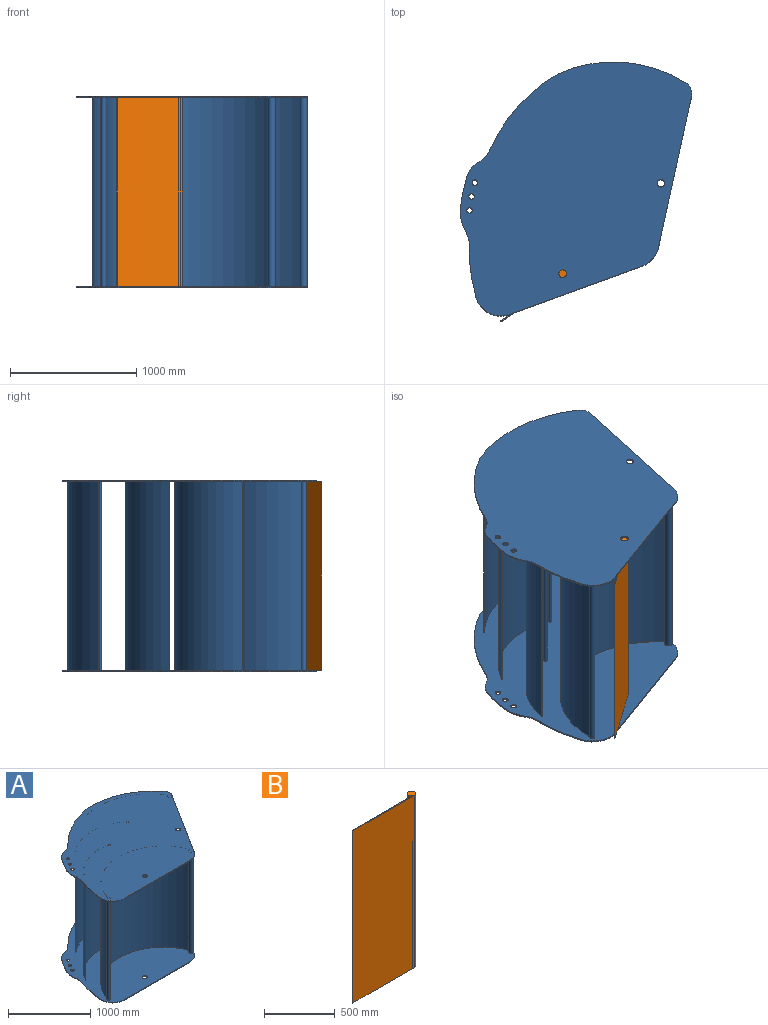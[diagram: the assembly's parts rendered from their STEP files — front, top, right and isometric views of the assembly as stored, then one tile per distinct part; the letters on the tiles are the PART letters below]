
ASSEMBLY  parts=2 mates=2
PART A: 61 faces, bbox 2164.2x1661x1520 mm
  f0: cylinder r=30.5mm len=61mm, axis (0,0,-1), area 1916.4mm2, adj f48,f49
  f1: cylinder r=29.5mm len=59mm, axis (0,0,-1), area 1853.5mm2, adj f48,f49
  f2: cylinder r=22mm len=44mm, axis (0,0,-1), area 1382.3mm2, adj f48,f49
  f3: cylinder r=22mm len=44mm, axis (0,0,-1), area 1382.3mm2, adj f48,f49
  f4: cylinder r=22mm len=44mm, axis (0,0,-1), area 1382.3mm2, adj f48,f49
  f5: cylinder r=326.18mm len=176.61mm, axis (0,0,-1), area 1797.7mm2, adj f48,f49,f50,f60
  f6: cylinder r=200mm len=212.82mm, axis (0,0,-1), area 3269.9mm2, adj f48,f49,f51,f52
  f7: cylinder r=20.5mm len=1500mm, axis (0,0,-1), area 183146.8mm2, adj f30,f44,f45,f49
  f8: cylinder r=30.5mm len=1500mm, axis (0,0,-1), area 272705.4mm2, adj f30,f44,f45,f46,f47,f49
  f9: cylinder r=15.5mm len=1500mm, axis (0,0,-1), area 135747.8mm2, adj f30,f41,f43,f49
  f10: cylinder r=15.5mm len=1500mm, axis (0,0,-1), area 136340.4mm2, adj f30,f37,f40,f49
  f11: cylinder r=30.5mm len=1500mm, axis (0,0,-1), area 274743.1mm2, adj f30,f32,f34,f35,f36,f49
  f12: cylinder r=30.5mm len=61mm, axis (0,0,-1), area 1916.4mm2, adj f30,f31
  f13: cylinder r=22mm len=44mm, axis (0,0,-1), area 1382.3mm2, adj f30,f31
  f14: cylinder r=22mm len=44mm, axis (0,0,-1), area 1382.3mm2, adj f30,f31
  f15: cylinder r=22mm len=44mm, axis (0,0,-1), area 1382.3mm2, adj f30,f31
  f16: cylinder r=29.5mm len=59mm, axis (0,0,-1), area 1853.5mm2, adj f30,f31
  f17: cylinder r=326.18mm len=176.61mm, axis (0,0,-1), area 1797.7mm2, adj f28,f29,f30,f31
  f18: cylinder r=200mm len=212.82mm, axis (0,0,-1), area 3269.9mm2, adj f19,f20,f30,f31
  f19: cylinder r=1403.06mm len=415.74mm, axis (0,0,-1), area 4273.2mm2, adj f18,f29,f30,f31
  f20: plane 1123.76x10mm, normal (0,-1,0), area 11237.6mm2, adj f18,f21,f30,f31
  f21: cylinder r=200mm len=169mm, axis (0,0,-1), area 2013.2mm2, adj f20,f22,f30,f31
  f22: plane 1036.5x655.9mm, normal (0.85,-0.53,0), area 12265.9mm2, adj f21,f23,f30,f31,f36,f47
  f23: cylinder r=100mm len=114.68mm, axis (0,0,-1), area 1222.9mm2, adj f22,f24,f30,f31
  f24: cylinder r=1074.34mm len=926.41mm, axis (0,0,-1), area 10568mm2, adj f23,f25,f30,f31
  f25: cylinder r=1282.61mm len=713.26mm, axis (0,0,-1), area 8227.7mm2, adj f24,f26,f30,f31
  f26: cylinder r=200mm len=117.51mm, axis (0,0,-1), area 1346.6mm2, adj f25,f27,f30,f31
  f27: cylinder r=186.95mm len=116.81mm, axis (0,0,-1), area 1363.1mm2, adj f26,f28,f30,f31
  f28: cylinder r=1324.47mm len=239.75mm, axis (0,0,-1), area 2828.3mm2, adj f17,f27,f30,f31
  f29: cylinder r=200mm len=107.43mm, axis (0,0,-1), area 1093.1mm2, adj f17,f19,f30,f31
  f30: plane 2164.16x1660.98mm, normal (0,0,1), area 2565292.9mm2, adj f7,f8,f9,f10,f11,f12,f13,f14
  f31: plane 2164.16x1660.98mm, normal (0,0,-1), area 2603609.2mm2, adj f12,f13,f14,f15,f16,f17,f18,f19
  f32: cylinder r=883.17mm len=1500mm, axis (0,0,-1), area 1936048.7mm2, adj f11,f30,f33,f49
  f33: plane 1500x5.5mm, normal (-0.92,-0.4,0), area 9000mm2, adj f30,f32,f34,f49
  f34: cylinder r=877.17mm len=1500mm, axis (0,0,-1), area 1914005.6mm2, adj f11,f30,f33,f49
  f35: plane 9.3x5.88mm, normal (0,0,1), area 3.7mm2, adj f11,f54
  f36: plane 9.3x5.88mm, normal (0,0,-1), area 3.7mm2, adj f11,f22
  f37: cylinder r=685.89mm len=1500mm, axis (0,0,-1), area 1444091.5mm2, adj f10,f30,f38,f49
  f38: plane 1500x4.62mm, normal (-0.77,-0.64,0), area 9000mm2, adj f30,f37,f39,f49
  f39: plane 1500x0.08mm, normal (0.65,-0.76,0), area 152.6mm2, adj f30,f38,f40,f49
  f40: cylinder r=679.89mm len=1500mm, axis (0,0,-1), area 1427930.9mm2, adj f10,f30,f39,f49
  f41: cylinder r=640.37mm len=1500mm, axis (0,0,-1), area 1242581.2mm2, adj f9,f30,f42,f49
  f42: plane 1500x5.24mm, normal (-0.49,-0.87,0), area 9000mm2, adj f30,f41,f43,f49
  f43: cylinder r=634.37mm len=1500mm, axis (0,0,-1), area 1226053.6mm2, adj f9,f30,f42,f49
  f44: cylinder r=755.25mm len=1500mm, axis (0,0,-1), area 2799788.5mm2, adj f7,f8,f30,f49
  f45: cylinder r=761.25mm len=1500mm, axis (0,0,-1), area 2838096.4mm2, adj f7,f8,f30,f49
  f46: plane 9.3x5.88mm, normal (0,0,1), area 3.7mm2, adj f8,f54
  f47: plane 9.3x5.88mm, normal (0,0,-1), area 3.7mm2, adj f8,f22
  f48: plane 2164.16x1660.98mm, normal (0,0,1), area 2603609.2mm2, adj f0,f1,f2,f3,f4,f5,f6,f50
  f49: plane 2164.16x1660.98mm, normal (0,0,-1), area 2565292.9mm2, adj f0,f1,f2,f3,f4,f5,f6,f7
  f50: cylinder r=200mm len=107.43mm, axis (0,0,-1), area 1093.1mm2, adj f5,f48,f49,f51
  f51: cylinder r=1403.06mm len=415.74mm, axis (0,0,-1), area 4273.2mm2, adj f6,f48,f49,f50
  f52: plane 1123.76x10mm, normal (0,-1,0), area 11237.6mm2, adj f6,f48,f49,f53
  f53: cylinder r=200mm len=169mm, axis (0,0,-1), area 2013.2mm2, adj f48,f49,f52,f54
  f54: plane 1036.5x655.9mm, normal (0.85,-0.53,0), area 12265.9mm2, adj f35,f46,f48,f49,f53,f55
  f55: cylinder r=100mm len=114.68mm, axis (0,0,-1), area 1222.9mm2, adj f48,f49,f54,f56
  f56: cylinder r=1074.34mm len=926.41mm, axis (0,0,-1), area 10568mm2, adj f48,f49,f55,f57
  f57: cylinder r=1282.61mm len=713.26mm, axis (0,0,-1), area 8227.7mm2, adj f48,f49,f56,f58
  f58: cylinder r=200mm len=117.51mm, axis (0,0,-1), area 1346.6mm2, adj f48,f49,f57,f59
  f59: cylinder r=186.95mm len=116.81mm, axis (0,0,-1), area 1363.1mm2, adj f48,f49,f58,f60
  f60: cylinder r=1324.47mm len=239.75mm, axis (0,0,-1), area 2828.3mm2, adj f5,f48,f49,f59
PART B: 6 faces, bbox 646.3x61x1490 mm
  f0: cylinder r=30.5mm len=1490mm, axis (0,0,-1), area 256544.7mm2, adj f1,f2,f4,f5
  f1: plane 1490x615.77mm, normal (0,-1,0), area 917501.9mm2, adj f0,f3,f4,f5
  f2: plane 1490x597.61mm, normal (0,1,0), area 890434.7mm2, adj f0,f3,f4,f5
  f3: plane 1490x6mm, normal (-1,0,0), area 8940mm2, adj f1,f2,f4,f5
  f4: plane 646.27x61mm, normal (0,0,1), area 6542.9mm2, adj f0,f1,f2,f3
  f5: plane 646.27x61mm, normal (0,0,-1), area 6542.9mm2, adj f0,f1,f2,f3
PLACE A rot(axis=(0,0,1),20deg) t=(0,0,-10)mm
PLACE B rot(axis=(0,0,1),35deg) t=(-211.98,176.74,-10)mm
MATE planar A.f0 <-> B.f0  axis (0,0,-1) through (-777.23,-716.71,750)mm
MATE revolute A.f0 <-> B.f0  axis (0,0,-1) through (-777.23,-716.71,750)mm
